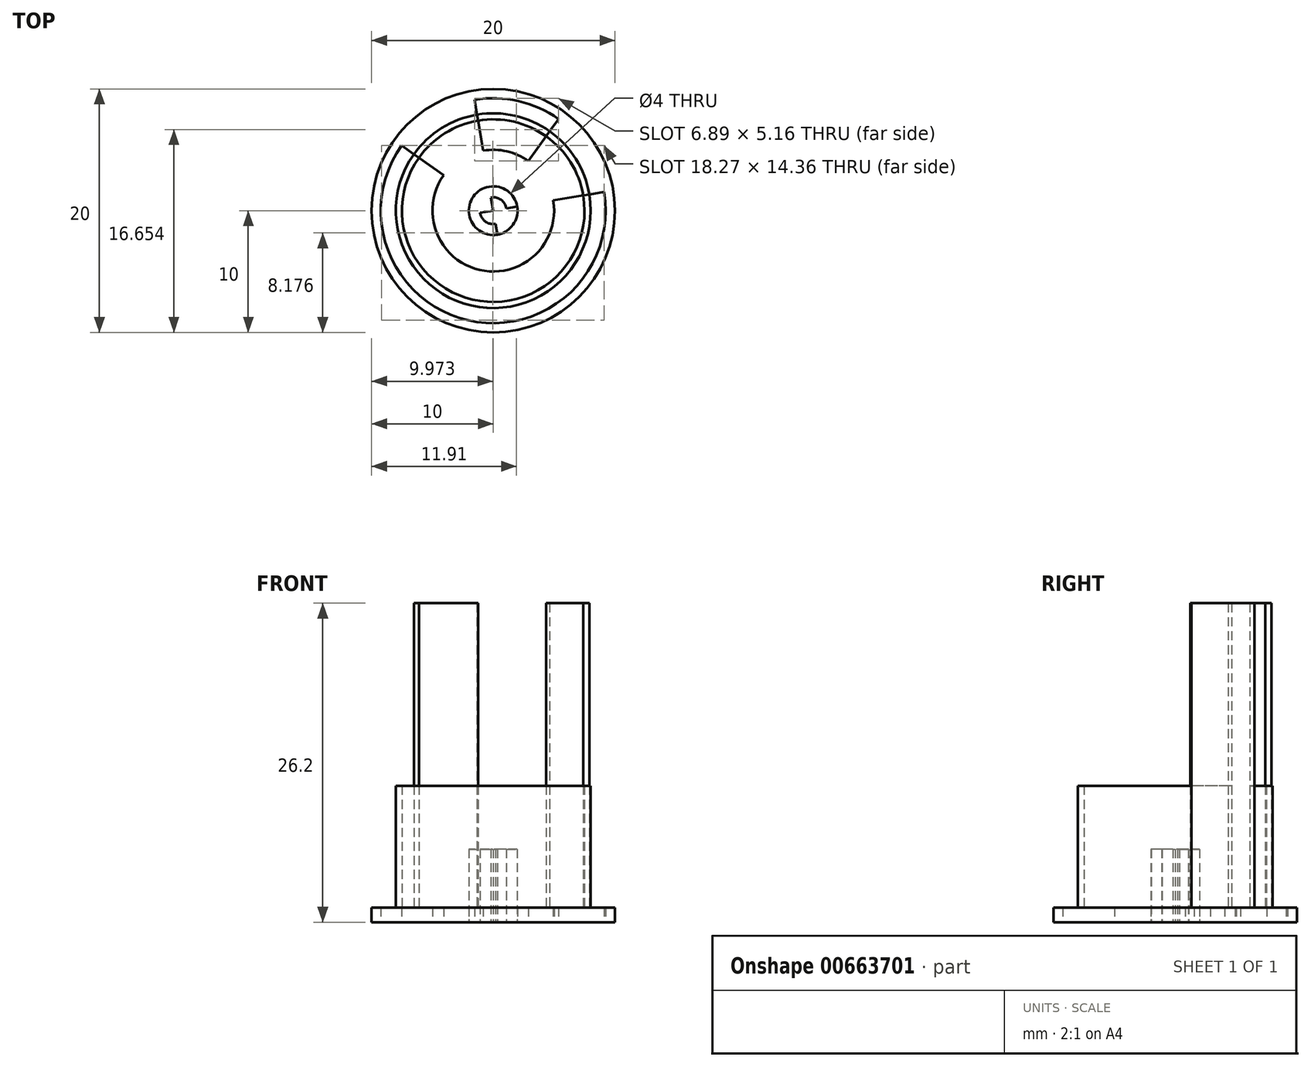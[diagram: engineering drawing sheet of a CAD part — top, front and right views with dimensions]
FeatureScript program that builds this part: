
annotation { "Feature Type Name" : "Feature", "Feature Type Description" : "" }
export const myFeature = defineFeature(function(context is Context, id is Id, definition is map)
    precondition{}
    {
        {
            var Q0;
            Q0=qCreatedBy(makeId("Top.planeOp"),FACE);
            var sketch = newSketch(context, id + "F0", { "sketchPlane" : qUnion([Q0])});
            skCircle(sketch, "E0", {"center": v(0, 0) * mm, "radius": 10 * mm});
            skCircle(sketch, "E1.cCircle", {"center": v(0, 0) * mm, "radius": 10 * mm, "construction": true});
            skLineSegment(sketch, "E1.0", {"start": v(5.8, 8.15) * mm, "end": v(9.86, 1.66) * mm});
            skLineSegment(sketch, "E1.1", {"start": v(9.86, 1.66) * mm, "end": v(8.15, -5.8) * mm});
            skLineSegment(sketch, "E1.2", {"start": v(8.15, -5.8) * mm, "end": v(1.66, -9.86) * mm});
            skLineSegment(sketch, "E1.3", {"start": v(1.66, -9.86) * mm, "end": v(-5.8, -8.15) * mm});
            skLineSegment(sketch, "E1.4", {"start": v(-5.8, -8.15) * mm, "end": v(-9.86, -1.66) * mm});
            skLineSegment(sketch, "E1.5", {"start": v(-9.86, -1.66) * mm, "end": v(-8.15, 5.8) * mm});
            skLineSegment(sketch, "E1.6", {"start": v(-8.15, 5.8) * mm, "end": v(-1.66, 9.86) * mm});
            skLineSegment(sketch, "E1.7", {"start": v(-1.66, 9.86) * mm, "end": v(5.8, 8.15) * mm});
            skLineSegment(sketch, "E2", {"start": v(-8.15, 5.8) * mm, "end": v(8.15, -5.8) * mm});
            skLineSegment(sketch, "E3", {"start": v(5.8, 8.15) * mm, "end": v(-5.8, -8.15) * mm});
            skLineSegment(sketch, "E4", {"start": v(-9.86, -1.66) * mm, "end": v(9.86, 1.66) * mm});
            skLineSegment(sketch, "E5", {"start": v(-1.66, 9.86) * mm, "end": v(1.66, -9.86) * mm});
            skCircle(sketch, "E6", {"center": v(0, 0) * mm, "radius": 5 * mm});
            skCircle(sketch, "E7", {"center": v(0, 0) * mm, "radius": 9.24 * mm});
            skCircle(sketch, "E8", {"center": v(0, 0) * mm, "radius": 7.5 * mm, "construction": true});
            skLineSegment(sketch, "E9", {"start": v(0, 0) * mm, "end": v(-2.07, -9) * mm, "construction": true});
            skLineSegment(sketch, "E10", {"start": v(-1.68, -7.3) * mm, "end": v(6.11, -4.35) * mm, "construction": true});
            skCircle(sketch, "E11", {"center": v(0, 0) * mm, "radius": 2 * mm});
            skCircle(sketch, "E12", {"center": v(0, 0) * mm, "radius": 1.1 * mm});
            skSolve(sketch);
        }
        {
            var Q0;
            Q0 = qSketchRegion(id + "F0", true);
            var Q1;
            {var subQ0=sQuery(id+"F0.wireOp",EDGE,"E6");var subQ1=sQuery(id+"F0.wireOp",EDGE,"E3");var subQ2=makeQuery(id+"F0.imprint","INTERSECT",VERTEX,{"disambiguationData":[OD(1.0)],"derivedFrom":[subQ1,subQ0]});Q1=makeQuery(id+"F0.imprint","IMPRINT",FACE,{"disambiguationData":[TD([[makeQuery(id+"F0.imprint","IMPRINT",EDGE,{"disambiguationData":[TD([[subQ2,1.0]])],"derivedFrom":subQ0}),1.0]])]});}
            var Q2;
            {var subQ0=sQuery(id+"F0.wireOp",EDGE,"E6");var subQ1=sQuery(id+"F0.wireOp",EDGE,"E2");var subQ2=makeQuery(id+"F0.imprint","INTERSECT",VERTEX,{"disambiguationData":[OD(0.0)],"derivedFrom":[subQ1,subQ0]});Q2=makeQuery(id+"F0.imprint","IMPRINT",FACE,{"disambiguationData":[TD([[makeQuery(id+"F0.imprint","IMPRINT",EDGE,{"disambiguationData":[TD([[subQ2,-1.0]])],"derivedFrom":subQ0}),1.0]])]});}
            var Q3;
            {var subQ0=sQuery(id+"F0.wireOp",EDGE,"E6");var subQ1=sQuery(id+"F0.wireOp",EDGE,"E2");var subQ2=makeQuery(id+"F0.imprint","INTERSECT",VERTEX,{"disambiguationData":[OD(0.0)],"derivedFrom":[subQ1,subQ0]});Q3=makeQuery(id+"F0.imprint","IMPRINT",FACE,{"disambiguationData":[TD([[makeQuery(id+"F0.imprint","IMPRINT",EDGE,{"disambiguationData":[TD([[subQ2,1.0]])],"derivedFrom":subQ0}),1.0]])]});}
            var Q4;
            {var subQ0=sQuery(id+"F0.wireOp",EDGE,"E6");var subQ1=sQuery(id+"F0.wireOp",EDGE,"E3");var subQ2=makeQuery(id+"F0.imprint","INTERSECT",VERTEX,{"disambiguationData":[OD(0.0)],"derivedFrom":[subQ1,subQ0]});Q4=makeQuery(id+"F0.imprint","IMPRINT",FACE,{"disambiguationData":[TD([[makeQuery(id+"F0.imprint","IMPRINT",EDGE,{"disambiguationData":[TD([[subQ2,-1.0]])],"derivedFrom":subQ0}),1.0]])]});}
            var Q5;
            {var subQ0=sQuery(id+"F0.wireOp",EDGE,"E6");var subQ1=sQuery(id+"F0.wireOp",EDGE,"E3");var subQ2=makeQuery(id+"F0.imprint","INTERSECT",VERTEX,{"disambiguationData":[OD(0.0)],"derivedFrom":[subQ1,subQ0]});Q5=makeQuery(id+"F0.imprint","IMPRINT",FACE,{"disambiguationData":[TD([[makeQuery(id+"F0.imprint","IMPRINT",EDGE,{"disambiguationData":[TD([[subQ2,1.0]])],"derivedFrom":subQ0}),1.0]])]});}
            var Q6;
            {var subQ0=sQuery(id+"F0.wireOp",EDGE,"E6");var subQ1=sQuery(id+"F0.wireOp",EDGE,"E2");var subQ2=makeQuery(id+"F0.imprint","INTERSECT",VERTEX,{"disambiguationData":[OD(1.0)],"derivedFrom":[subQ1,subQ0]});Q6=makeQuery(id+"F0.imprint","IMPRINT",FACE,{"disambiguationData":[TD([[makeQuery(id+"F0.imprint","IMPRINT",EDGE,{"disambiguationData":[TD([[subQ2,-1.0]])],"derivedFrom":subQ0}),1.0]])]});}
            var Q7;
            {var subQ0=sQuery(id+"F0.wireOp",EDGE,"E6");var subQ1=sQuery(id+"F0.wireOp",EDGE,"E2");var subQ2=makeQuery(id+"F0.imprint","INTERSECT",VERTEX,{"disambiguationData":[OD(1.0)],"derivedFrom":[subQ1,subQ0]});Q7=makeQuery(id+"F0.imprint","IMPRINT",FACE,{"disambiguationData":[TD([[makeQuery(id+"F0.imprint","IMPRINT",EDGE,{"disambiguationData":[TD([[subQ2,1.0]])],"derivedFrom":subQ0}),1.0]])]});}
            var Q8;
            {var subQ0=sQuery(id+"F0.wireOp",EDGE,"E6");var subQ1=sQuery(id+"F0.wireOp",EDGE,"E3");var subQ2=makeQuery(id+"F0.imprint","INTERSECT",VERTEX,{"disambiguationData":[OD(1.0)],"derivedFrom":[subQ1,subQ0]});Q8=makeQuery(id+"F0.imprint","IMPRINT",FACE,{"disambiguationData":[TD([[makeQuery(id+"F0.imprint","IMPRINT",EDGE,{"disambiguationData":[TD([[subQ2,-1.0]])],"derivedFrom":subQ0}),1.0]])]});}
            var Q9;
            {var subQ0=sQuery(id+"F0.wireOp",EDGE,"E6");var subQ1=sQuery(id+"F0.wireOp",EDGE,"E2");var subQ2=makeQuery(id+"F0.imprint","INTERSECT",VERTEX,{"disambiguationData":[OD(1.0)],"derivedFrom":[subQ1,subQ0]});Q9=makeQuery(id+"F0.imprint","IMPRINT",FACE,{"disambiguationData":[TD([[makeQuery(id+"F0.imprint","IMPRINT",EDGE,{"disambiguationData":[TD([[subQ2,-1.0]])],"derivedFrom":subQ1}),-1.0]])]});}
            var Q10;
            {var subQ1=sQuery(id+"F0.wireOp",EDGE,"E3");var subQ5=sQuery(id+"F0.wireOp",EDGE,"E7");var subQ8=makeQuery(id+"F0.imprint","INTERSECT",VERTEX,{"disambiguationData":[OD(0.0)],"derivedFrom":[subQ1,subQ5]});Q10=makeQuery(id+"F0.imprint","IMPRINT",FACE,{"disambiguationData":[TD([[makeQuery(id+"F0.imprint","IMPRINT",EDGE,{"disambiguationData":[TD([[subQ8,-1.0]])],"derivedFrom":subQ1}),1.0]])]});}
            var Q11;
            {var subQ0=sQuery(id+"F0.wireOp",EDGE,"E7");var subQ6=sQuery(id+"F0.wireOp",EDGE,"E2");var subQ8=makeQuery(id+"F0.imprint","INTERSECT",VERTEX,{"disambiguationData":[OD(0.0)],"derivedFrom":[subQ6,subQ0]});Q11=makeQuery(id+"F0.imprint","IMPRINT",FACE,{"disambiguationData":[TD([[makeQuery(id+"F0.imprint","IMPRINT",EDGE,{"disambiguationData":[TD([[subQ8,-1.0]])],"derivedFrom":subQ6}),1.0]])]});}
            var Q12;
            {var subQ0=sQuery(id+"F0.wireOp",EDGE,"E6");var subQ1=sQuery(id+"F0.wireOp",EDGE,"E3");var subQ2=makeQuery(id+"F0.imprint","INTERSECT",VERTEX,{"disambiguationData":[OD(1.0)],"derivedFrom":[subQ1,subQ0]});Q12=makeQuery(id+"F0.imprint","IMPRINT",FACE,{"disambiguationData":[TD([[makeQuery(id+"F0.imprint","IMPRINT",EDGE,{"disambiguationData":[TD([[subQ2,-1.0]])],"derivedFrom":subQ1}),-1.0]])]});}
            extrude(context, id + "F1", {"entities" : qUnion([Q0, Q1, Q2, Q3, Q4, Q5, Q6, Q7, Q8, Q9, Q10, Q11, Q12]), "depth" : 1.2 * mm, "offsetDistance" : 25 * mm});
        }
        {
            var Q0;
            {var subQ0=sQuery(id+"F0.wireOp",EDGE,"E11");var subQ1=sQuery(id+"F0.wireOp",EDGE,"E2");var subQ2=makeQuery(id+"F0.imprint","INTERSECT",VERTEX,{"disambiguationData":[OD(0.0)],"derivedFrom":[subQ1,subQ0]});Q0=makeQuery(id+"F0.imprint","IMPRINT",FACE,{"disambiguationData":[TD([[makeQuery(id+"F0.imprint","IMPRINT",EDGE,{"disambiguationData":[TD([[subQ2,-1.0]])],"derivedFrom":subQ1}),1.0]])]});}
            var Q1;
            {var subQ0=sQuery(id+"F0.wireOp",EDGE,"E11");var subQ1=sQuery(id+"F0.wireOp",EDGE,"E2");var subQ2=makeQuery(id+"F0.imprint","INTERSECT",VERTEX,{"disambiguationData":[OD(0.0)],"derivedFrom":[subQ1,subQ0]});Q1=makeQuery(id+"F0.imprint","IMPRINT",FACE,{"disambiguationData":[TD([[makeQuery(id+"F0.imprint","IMPRINT",EDGE,{"disambiguationData":[TD([[subQ2,-1.0]])],"derivedFrom":subQ1}),-1.0]])]});}
            var Q2;
            {var subQ0=sQuery(id+"F0.wireOp",EDGE,"E12");var subQ1=sQuery(id+"F0.wireOp",EDGE,"E3");var subQ2=makeQuery(id+"F0.imprint","INTERSECT",VERTEX,{"disambiguationData":[OD(1.0)],"derivedFrom":[subQ1,subQ0]});Q2=makeQuery(id+"F0.imprint","IMPRINT",FACE,{"disambiguationData":[TD([[makeQuery(id+"F0.imprint","IMPRINT",EDGE,{"disambiguationData":[TD([[subQ2,-1.0]])],"derivedFrom":subQ1}),-1.0]])]});}
            var Q3;
            {var subQ0=sQuery(id+"F0.wireOp",EDGE,"E12");var subQ1=sQuery(id+"F0.wireOp",EDGE,"E3");var subQ2=makeQuery(id+"F0.imprint","INTERSECT",VERTEX,{"disambiguationData":[OD(1.0)],"derivedFrom":[subQ1,subQ0]});Q3=makeQuery(id+"F0.imprint","IMPRINT",FACE,{"disambiguationData":[TD([[makeQuery(id+"F0.imprint","IMPRINT",EDGE,{"disambiguationData":[TD([[subQ2,-1.0]])],"derivedFrom":subQ1}),1.0]])]});}
            var Q4;
            {var subQ0=sQuery(id+"F0.wireOp",EDGE,"E12");var subQ1=sQuery(id+"F0.wireOp",EDGE,"E2");var subQ2=makeQuery(id+"F0.imprint","INTERSECT",VERTEX,{"disambiguationData":[OD(1.0)],"derivedFrom":[subQ1,subQ0]});Q4=makeQuery(id+"F0.imprint","IMPRINT",FACE,{"disambiguationData":[TD([[makeQuery(id+"F0.imprint","IMPRINT",EDGE,{"disambiguationData":[TD([[subQ2,-1.0]])],"derivedFrom":subQ1}),-1.0]])]});}
            var Q5;
            {var subQ0=sQuery(id+"F0.wireOp",EDGE,"E12");var subQ1=sQuery(id+"F0.wireOp",EDGE,"E2");var subQ2=makeQuery(id+"F0.imprint","INTERSECT",VERTEX,{"disambiguationData":[OD(1.0)],"derivedFrom":[subQ1,subQ0]});Q5=makeQuery(id+"F0.imprint","IMPRINT",FACE,{"disambiguationData":[TD([[makeQuery(id+"F0.imprint","IMPRINT",EDGE,{"disambiguationData":[TD([[subQ2,-1.0]])],"derivedFrom":subQ1}),1.0]])]});}
            var Q6;
            {var subQ0=sQuery(id+"F0.wireOp",EDGE,"E11");var subQ1=sQuery(id+"F0.wireOp",EDGE,"E3");var subQ2=makeQuery(id+"F0.imprint","INTERSECT",VERTEX,{"disambiguationData":[OD(0.0)],"derivedFrom":[subQ1,subQ0]});Q6=makeQuery(id+"F0.imprint","IMPRINT",FACE,{"disambiguationData":[TD([[makeQuery(id+"F0.imprint","IMPRINT",EDGE,{"disambiguationData":[TD([[subQ2,-1.0]])],"derivedFrom":subQ1}),1.0]])]});}
            var Q7;
            {var subQ0=sQuery(id+"F0.wireOp",EDGE,"E11");var subQ1=sQuery(id+"F0.wireOp",EDGE,"E3");var subQ2=makeQuery(id+"F0.imprint","INTERSECT",VERTEX,{"disambiguationData":[OD(0.0)],"derivedFrom":[subQ1,subQ0]});Q7=makeQuery(id+"F0.imprint","IMPRINT",FACE,{"disambiguationData":[TD([[makeQuery(id+"F0.imprint","IMPRINT",EDGE,{"disambiguationData":[TD([[subQ2,-1.0]])],"derivedFrom":subQ1}),-1.0]])]});}
            extrude(context, id + "F2", {"entities" : qUnion([Q0, Q1, Q2, Q3, Q4, Q5, Q6, Q7]), "depth" : 6 * mm, "offsetDistance" : 25 * mm});
        }
        {
            var Q0;
            Q0=makeQuery(id+"F1.opExtrude","CAP_FACE",FACE,{"disambiguationData":[OSD([sQuery(id+"F0.wireOp",EDGE,"E0"),sQuery(id+"F0.wireOp",EDGE,"E2"),sQuery(id+"F0.wireOp",EDGE,"E3"),sQuery(id+"F0.wireOp",EDGE,"E4"),sQuery(id+"F0.wireOp",EDGE,"E5"),sQuery(id+"F0.wireOp",EDGE,"E6"),sQuery(id+"F0.wireOp",EDGE,"E7"),sQuery(id+"F0.wireOp",EDGE,"E11")])],"isStart":false});
            var sketch = newSketch(context, id + "F3", { "sketchPlane" : qUnion([Q0])});
            skCircle(sketch, "E13.0", {"center": v(0, 0) * mm, "radius": 7.5 * mm});
            skCircle(sketch, "E14.0", {"center": v(0, 0) * mm, "radius": 8 * mm});
            skSolve(sketch);
        }
        {
            var Q0;
            {var subQ0=sQuery(id+"F3.wireOp",EDGE,"E13.0");var subQ1=sQuery(id+"F0.wireOp",EDGE,"E6");var subQ2=sQuery(id+"F0.wireOp",EDGE,"E5");var subQ4=makeQuery(id+"F1.opExtrude","CAP_EDGE",EDGE,{"disambiguationData":[OSD([subQ2]),TDD([makeQuery(id+"F0.imprint","IMPRINT",EDGE,{"disambiguationData":[TD([[makeQuery(id+"F0.imprint","INTERSECT",VERTEX,{"disambiguationData":[OD(1.0)],"derivedFrom":[subQ2,subQ1]}),-1.0]])],"derivedFrom":subQ2})])],"isStart":false});var subQ5=makeQuery(id+"F3.imprint","INTERSECT",VERTEX,{"derivedFrom":[subQ4,subQ0]});Q0=makeQuery(id+"F3.imprint","IMPRINT",FACE,{"disambiguationData":[TD([[makeQuery(id+"F3.imprint","IMPRINT",EDGE,{"disambiguationData":[TD([[subQ5,-1.0]])],"derivedFrom":subQ0}),-1.0]])]});}
            var Q1;
            {var subQ0=sQuery(id+"F3.wireOp",EDGE,"E13.0");var subQ1=sQuery(id+"F0.wireOp",EDGE,"E7");var subQ2=sQuery(id+"F0.wireOp",EDGE,"E5");var subQ4=makeQuery(id+"F1.opExtrude","CAP_EDGE",EDGE,{"disambiguationData":[OSD([subQ2]),TDD([makeQuery(id+"F0.imprint","IMPRINT",EDGE,{"disambiguationData":[TD([[makeQuery(id+"F0.imprint","INTERSECT",VERTEX,{"disambiguationData":[OD(0.0)],"derivedFrom":[subQ2,subQ1]}),-1.0]])],"derivedFrom":subQ2})])],"isStart":false});var subQ5=makeQuery(id+"F3.imprint","INTERSECT",VERTEX,{"derivedFrom":[subQ4,subQ0]});Q1=makeQuery(id+"F3.imprint","IMPRINT",FACE,{"disambiguationData":[TD([[makeQuery(id+"F3.imprint","IMPRINT",EDGE,{"disambiguationData":[TD([[subQ5,-1.0]])],"derivedFrom":subQ0}),-1.0]])]});}
            var Q2;
            {var subQ0=sQuery(id+"F3.wireOp",EDGE,"E13.0");var subQ1=sQuery(id+"F0.wireOp",EDGE,"E7");var subQ2=sQuery(id+"F0.wireOp",EDGE,"E3");var subQ4=makeQuery(id+"F1.opExtrude","CAP_EDGE",EDGE,{"disambiguationData":[OSD([subQ2]),TDD([makeQuery(id+"F0.imprint","IMPRINT",EDGE,{"disambiguationData":[TD([[makeQuery(id+"F0.imprint","INTERSECT",VERTEX,{"disambiguationData":[OD(0.0)],"derivedFrom":[subQ2,subQ1]}),-1.0]])],"derivedFrom":subQ2})])],"isStart":false});var subQ5=makeQuery(id+"F3.imprint","INTERSECT",VERTEX,{"derivedFrom":[subQ4,subQ0]});Q2=makeQuery(id+"F3.imprint","IMPRINT",FACE,{"disambiguationData":[TD([[makeQuery(id+"F3.imprint","IMPRINT",EDGE,{"disambiguationData":[TD([[subQ5,1.0]])],"derivedFrom":subQ0}),-1.0]])]});}
            var Q3;
            {var subQ0=sQuery(id+"F3.wireOp",EDGE,"E13.0");var subQ1=sQuery(id+"F0.wireOp",EDGE,"E7");var subQ2=sQuery(id+"F0.wireOp",EDGE,"E4");var subQ4=makeQuery(id+"F1.opExtrude","CAP_EDGE",EDGE,{"disambiguationData":[OSD([subQ2]),TDD([makeQuery(id+"F0.imprint","IMPRINT",EDGE,{"disambiguationData":[TD([[makeQuery(id+"F0.imprint","INTERSECT",VERTEX,{"disambiguationData":[OD(0.0)],"derivedFrom":[subQ2,subQ1]}),-1.0]])],"derivedFrom":subQ2})])],"isStart":false});var subQ5=makeQuery(id+"F3.imprint","INTERSECT",VERTEX,{"derivedFrom":[subQ4,subQ0]});Q3=makeQuery(id+"F3.imprint","IMPRINT",FACE,{"disambiguationData":[TD([[makeQuery(id+"F3.imprint","IMPRINT",EDGE,{"disambiguationData":[TD([[subQ5,-1.0]])],"derivedFrom":subQ0}),-1.0]])]});}
            extrude(context, id + "F4", {"entities" : qUnion([Q0, Q1, Q2, Q3]), "depth" : 25 * mm, "offsetDistance" : 25 * mm});
        }
        {
            var Q0;
            {var subQ0=sQuery(id+"F3.wireOp",EDGE,"E13.0");var subQ1=sQuery(id+"F0.wireOp",EDGE,"E6");var subQ2=sQuery(id+"F0.wireOp",EDGE,"E3");var subQ4=makeQuery(id+"F1.opExtrude","CAP_EDGE",EDGE,{"disambiguationData":[OSD([subQ2]),TDD([makeQuery(id+"F0.imprint","IMPRINT",EDGE,{"disambiguationData":[TD([[makeQuery(id+"F0.imprint","INTERSECT",VERTEX,{"disambiguationData":[OD(1.0)],"derivedFrom":[subQ2,subQ1]}),-1.0]])],"derivedFrom":subQ2})])],"isStart":false});var subQ5=makeQuery(id+"F3.imprint","INTERSECT",VERTEX,{"derivedFrom":[subQ4,subQ0]});Q0=makeQuery(id+"F3.imprint","IMPRINT",FACE,{"disambiguationData":[TD([[makeQuery(id+"F3.imprint","IMPRINT",EDGE,{"disambiguationData":[TD([[subQ5,-1.0]])],"derivedFrom":subQ0}),-1.0]])]});}
            var Q1;
            {var subQ0=sQuery(id+"F3.wireOp",EDGE,"E13.0");var subQ1=sQuery(id+"F0.wireOp",EDGE,"E6");var subQ2=sQuery(id+"F0.wireOp",EDGE,"E4");var subQ4=makeQuery(id+"F1.opExtrude","CAP_EDGE",EDGE,{"disambiguationData":[OSD([subQ2]),TDD([makeQuery(id+"F0.imprint","IMPRINT",EDGE,{"disambiguationData":[TD([[makeQuery(id+"F0.imprint","INTERSECT",VERTEX,{"disambiguationData":[OD(1.0)],"derivedFrom":[subQ2,subQ1]}),-1.0]])],"derivedFrom":subQ2})])],"isStart":false});var subQ5=makeQuery(id+"F3.imprint","INTERSECT",VERTEX,{"derivedFrom":[subQ4,subQ0]});Q1=makeQuery(id+"F3.imprint","IMPRINT",FACE,{"disambiguationData":[TD([[makeQuery(id+"F3.imprint","IMPRINT",EDGE,{"disambiguationData":[TD([[subQ5,1.0]])],"derivedFrom":subQ0}),-1.0]])]});}
            var Q2;
            {var subQ0=sQuery(id+"F3.wireOp",EDGE,"E13.0");var subQ1=sQuery(id+"F0.wireOp",EDGE,"E7");var subQ2=sQuery(id+"F0.wireOp",EDGE,"E3");var subQ4=makeQuery(id+"F1.opExtrude","CAP_EDGE",EDGE,{"disambiguationData":[OSD([subQ2]),TDD([makeQuery(id+"F0.imprint","IMPRINT",EDGE,{"disambiguationData":[TD([[makeQuery(id+"F0.imprint","INTERSECT",VERTEX,{"disambiguationData":[OD(0.0)],"derivedFrom":[subQ2,subQ1]}),-1.0]])],"derivedFrom":subQ2})])],"isStart":false});var subQ5=makeQuery(id+"F3.imprint","INTERSECT",VERTEX,{"derivedFrom":[subQ4,subQ0]});Q2=makeQuery(id+"F3.imprint","IMPRINT",FACE,{"disambiguationData":[TD([[makeQuery(id+"F3.imprint","IMPRINT",EDGE,{"disambiguationData":[TD([[subQ5,-1.0]])],"derivedFrom":subQ0}),-1.0]])]});}
            var Q3;
            {var subQ0=sQuery(id+"F3.wireOp",EDGE,"E13.0");var subQ1=sQuery(id+"F0.wireOp",EDGE,"E7");var subQ2=sQuery(id+"F0.wireOp",EDGE,"E2");var subQ4=makeQuery(id+"F1.opExtrude","CAP_EDGE",EDGE,{"disambiguationData":[OSD([subQ2]),TDD([makeQuery(id+"F0.imprint","IMPRINT",EDGE,{"disambiguationData":[TD([[makeQuery(id+"F0.imprint","INTERSECT",VERTEX,{"disambiguationData":[OD(0.0)],"derivedFrom":[subQ2,subQ1]}),-1.0]])],"derivedFrom":subQ2})])],"isStart":false});var subQ5=makeQuery(id+"F3.imprint","INTERSECT",VERTEX,{"derivedFrom":[subQ4,subQ0]});Q3=makeQuery(id+"F3.imprint","IMPRINT",FACE,{"disambiguationData":[TD([[makeQuery(id+"F3.imprint","IMPRINT",EDGE,{"disambiguationData":[TD([[subQ5,-1.0]])],"derivedFrom":subQ0}),-1.0]])]});}
            extrude(context, id + "F5", {"entities" : qUnion([Q0, Q1, Q2, Q3]), "depth" : 10 * mm, "offsetDistance" : 25 * mm});
        }
    });
